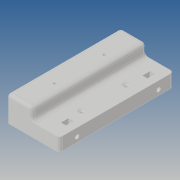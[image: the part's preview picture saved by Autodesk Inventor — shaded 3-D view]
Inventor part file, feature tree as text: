
AUTODESK INVENTOR PART (.ipt)
format: ipt  version: 2020 (Build 240168000, 168)  size: 264,704 bytes
history: native  units: in
note: dims shown in document units (in); Inventor stores cm internally (conversion verified against a paired STEP export)
features: other x7, extrude x7, sketch x7, reference x4, fillet x2, chamfer x1, projected_geometry x1
ambient origin geometry x8: Origin, YZ Plane, XZ Plane, XY Plane, X Axis, Y Axis, Z Axis, Center Point
bodies: Body1 (feature_tree)
feature tree (29):
  other  "Твердое тело1"
  extrude  "Выдавливание1"  Depth=0.1181in TaperAngle=0.0deg
  extrude  "Выдавливание2"  Depth=0.1181in TaperAngle=0.0deg
  sketch  "Эскиз3"
  other  "РабПлоскость1"
  extrude  "Выдавливание3"  Depth=0.1181in TaperAngle=0.0deg
  other  "Толщина1"
  fillet  "Сопряжение1"  Radius=0.1in
  extrude  "Выдавливание4"  Depth=0.1in
  fillet  "Сопряжение2"  Radius=0.125in
  chamfer  "Фаска1"  Distance=0.315in
  extrude  "Выдавливание5"  Depth=0.315in
  extrude  "Выдавливание6"  Depth=0.3937in TaperAngle=0.0deg
  extrude  "Выдавливание7"  Depth=0.125in
  sketch  "Эскиз2"
  reference  "Ссылка1"
  reference  "Ссылка2"
  reference  "Ссылка3"
  reference  "Ссылка4"
  sketch  "Эскиз4"
  sketch  "Эскиз5"
  projected_geometry  "Спроецированная петля1"
  sketch  "Эскиз6"
  sketch  "Эскиз7"
  sketch  "Эскиз1"
  parser-record x1  (decoder bookkeeping rows leaked as tree rows — omitted from the tree; the rows remain in map.json)
  other  "realsenses_plate_v2.ipt.iam"
  other  "Intel RealSense T265:1"
  other  "body:1"
note: 1 file-system path scrubbed to <path> (originals preserved in map.json)
